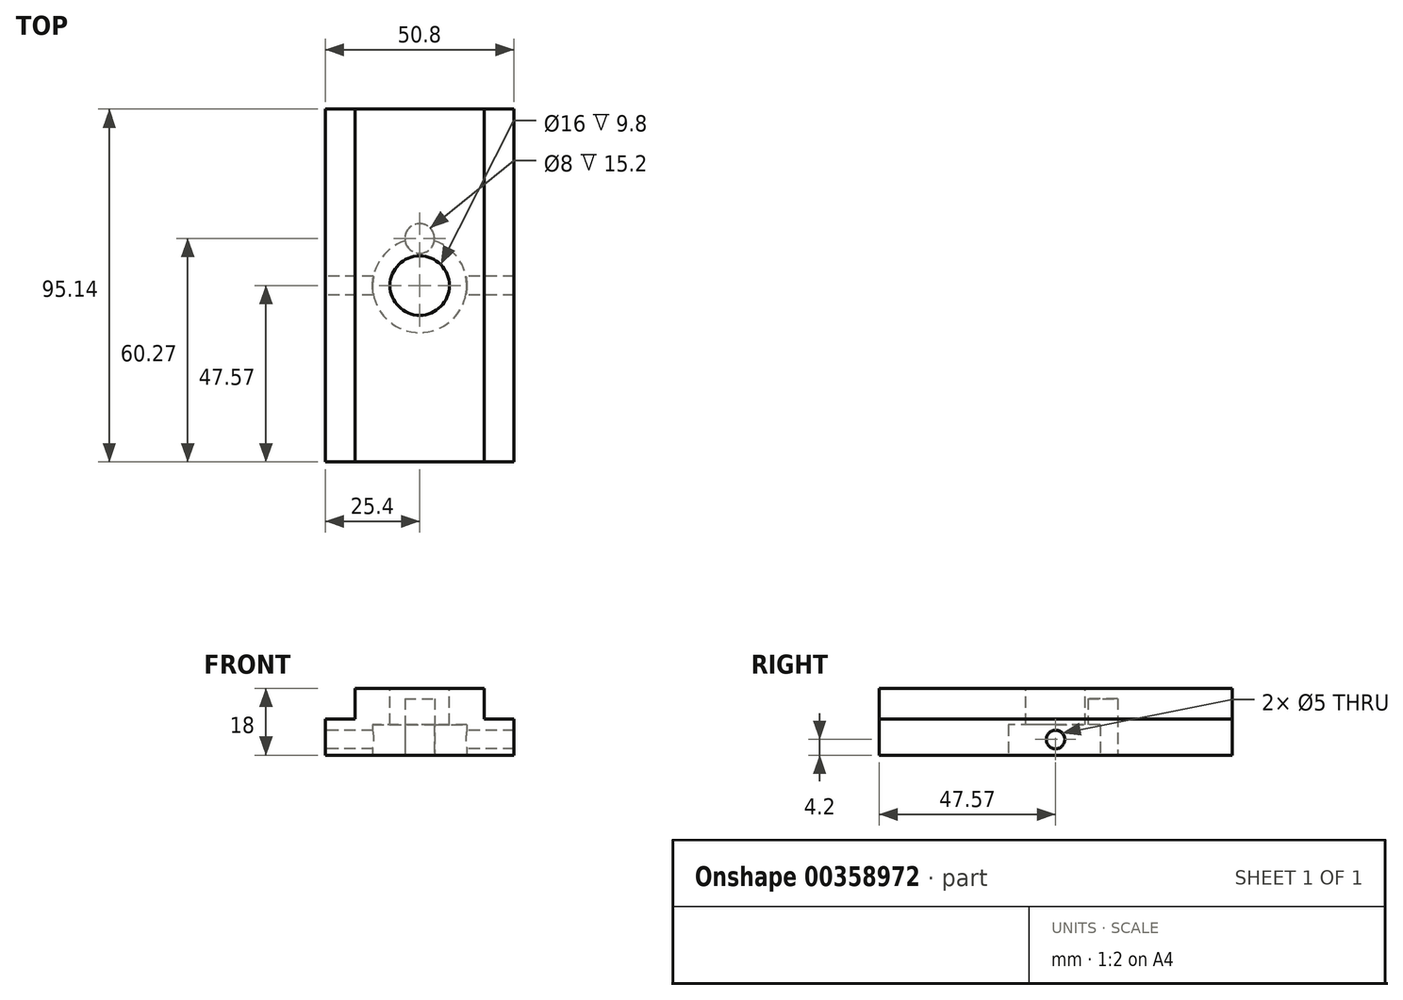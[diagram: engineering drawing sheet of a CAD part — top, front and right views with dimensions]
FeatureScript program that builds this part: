
annotation { "Feature Type Name" : "Feature", "Feature Type Description" : "" }
export const myFeature = defineFeature(function(context is Context, id is Id, definition is map)
    precondition{}
    {
        {
            var Q0;
            Q0=qCreatedBy(makeId("Front.planeOp"),FACE);
            var sketch = newSketch(context, id + "F0", { "sketchPlane" : qUnion([Q0])});
            skLineSegment(sketch, "E0", {"start": v(0, 0) * mm, "end": v(25.4, 0) * mm});
            skLineSegment(sketch, "E1", {"start": v(25.4, 0) * mm, "end": v(25.4, 9.66) * mm});
            skLineSegment(sketch, "E2", {"start": v(25.4, 9.66) * mm, "end": v(17.44, 9.66) * mm});
            skLineSegment(sketch, "E3", {"start": v(17.44, 9.66) * mm, "end": v(17.44, 18) * mm});
            skLineSegment(sketch, "E4", {"start": v(17.44, 18) * mm, "end": v(0, 18) * mm});
            skLineSegment(sketch, "E5", {"start": v(0, 32.83) * mm, "end": v(0, -18.5) * mm, "construction": true});
            skLineSegment(sketch, "E6.MirrorCS", {"start": v(-17.44, 9.66) * mm, "end": v(-17.44, 18) * mm});
            skLineSegment(sketch, "E7.MirrorCS", {"start": v(-25.4, 0) * mm, "end": v(-25.4, 9.66) * mm});
            skLineSegment(sketch, "E8.MirrorCS", {"start": v(-25.4, 9.66) * mm, "end": v(-17.44, 9.66) * mm});
            skLineSegment(sketch, "E9.MirrorCS", {"start": v(-17.44, 18) * mm, "end": v(0, 18) * mm});
            skLineSegment(sketch, "E10.MirrorCS", {"start": v(0, 0) * mm, "end": v(-25.4, 0) * mm});
            skSolve(sketch);
        }
        {
            var Q0;
            Q0 = qSketchRegion(id + "F0", true);
            extrude(context, id + "F1", {"entities" : qUnion([Q0]), "depth" : 95.14 * mm, "symmetric" : true});
        }
        {
            var Q0;
            Q0=makeQuery(id+"F1.opExtrude","SWEPT_FACE",FACE,{"disambiguationData":[OSD([sQuery(id+"F0.wireOp",EDGE,"E4"),sQuery(id+"F0.wireOp",EDGE,"E9.MirrorCS")])]});
            var sketch = newSketch(context, id + "F2", { "sketchPlane" : qUnion([Q0])});
            skCircle(sketch, "E11", {"center": v(0, 0) * mm, "radius": 8 * mm});
            skLineSegment(sketch, "E12.top", {"start": v(17.44, 5) * mm, "end": v(28.95, 5) * mm, "construction": true});
            skLineSegment(sketch, "E12.left", {"start": v(17.44, 0) * mm, "end": v(17.44, 5) * mm, "construction": true});
            skLineSegment(sketch, "E12.right", {"start": v(28.95, 0) * mm, "end": v(28.95, 5) * mm, "construction": true});
            skLineSegment(sketch, "E13.MirrorCS", {"start": v(17.44, 0) * mm, "end": v(17.44, -5) * mm, "construction": true});
            skLineSegment(sketch, "E14.MirrorCS", {"start": v(17.44, -5) * mm, "end": v(28.95, -5) * mm, "construction": true});
            skLineSegment(sketch, "E15.MirrorCS", {"start": v(28.95, 0) * mm, "end": v(28.95, -5) * mm, "construction": true});
            skLineSegment(sketch, "E16.MirrorCS", {"start": v(-28.95, 0) * mm, "end": v(-28.95, 5) * mm, "construction": true});
            skLineSegment(sketch, "E17.MirrorCS", {"start": v(-17.44, 5) * mm, "end": v(-28.95, 5) * mm, "construction": true});
            skLineSegment(sketch, "E18.MirrorCS", {"start": v(-17.44, 0) * mm, "end": v(-17.44, 5) * mm, "construction": true});
            skLineSegment(sketch, "E19.MirrorCS", {"start": v(-17.44, 0) * mm, "end": v(-17.44, -5) * mm, "construction": true});
            skLineSegment(sketch, "E20.MirrorCS", {"start": v(-28.95, 0) * mm, "end": v(-28.95, -5) * mm, "construction": true});
            skLineSegment(sketch, "E21.MirrorCS", {"start": v(-17.44, -5) * mm, "end": v(-28.95, -5) * mm, "construction": true});
            skSolve(sketch);
        }
        {
            var Q0;
            Q0 = qSketchRegion(id + "F2", true);
            extrude(context, id + "F3", {"entities" : qUnion([Q0]), "operationType" : NewBodyOperationType.REMOVE, "oppositeDirection" : true, "depth" : 25 * mm});
        }
        {
            var Q0;
            Q0=makeQuery(id+"F1.opExtrude","SWEPT_FACE",FACE,{"disambiguationData":[OSD([sQuery(id+"F0.wireOp",EDGE,"E0"),sQuery(id+"F0.wireOp",EDGE,"E10.MirrorCS")])]});
            var sketch = newSketch(context, id + "F4", { "sketchPlane" : qUnion([Q0])});
            skCircle(sketch, "E22", {"center": v(0, 0) * mm, "radius": 12.7 * mm});
            skSolve(sketch);
        }
        {
            var Q0;
            Q0 = qSketchRegion(id + "F4", true);
            extrude(context, id + "F5", {"entities" : qUnion([Q0]), "operationType" : NewBodyOperationType.REMOVE, "oppositeDirection" : true, "depth" : 8.2 * mm});
        }
        {
            var Q0;
            Q0=makeQuery(id+"F1.opExtrude","SWEPT_FACE",FACE,{"disambiguationData":[OSD([sQuery(id+"F0.wireOp",EDGE,"E7.MirrorCS")])]});
            var sketch = newSketch(context, id + "F6", { "sketchPlane" : qUnion([Q0])});
            skCircle(sketch, "E23", {"center": v(0, 4.2) * mm, "radius": 2.5 * mm});
            skSolve(sketch);
        }
        {
            var Q0;
            Q0 = qSketchRegion(id + "F6", true);
            extrude(context, id + "F7", {"entities" : qUnion([Q0]), "operationType" : NewBodyOperationType.REMOVE, "endBound" : BoundingType.THROUGH_ALL, "oppositeDirection" : true, "depth" : 25 * mm});
        }
        {
            var Q0;
            Q0=makeQuery(id+"F1.opExtrude","SWEPT_FACE",FACE,{"disambiguationData":[OSD([sQuery(id+"F0.wireOp",EDGE,"E0"),sQuery(id+"F0.wireOp",EDGE,"E10.MirrorCS")])]});
            var sketch = newSketch(context, id + "F8", { "sketchPlane" : qUnion([Q0])});
            skCircle(sketch, "E24", {"center": v(0, -12.7) * mm, "radius": 4 * mm});
            skSolve(sketch);
        }
        {
            var Q0;
            Q0 = qSketchRegion(id + "F8", true);
            extrude(context, id + "F9", {"entities" : qUnion([Q0]), "operationType" : NewBodyOperationType.REMOVE, "oppositeDirection" : true, "depth" : 15.2 * mm});
        }
    });
